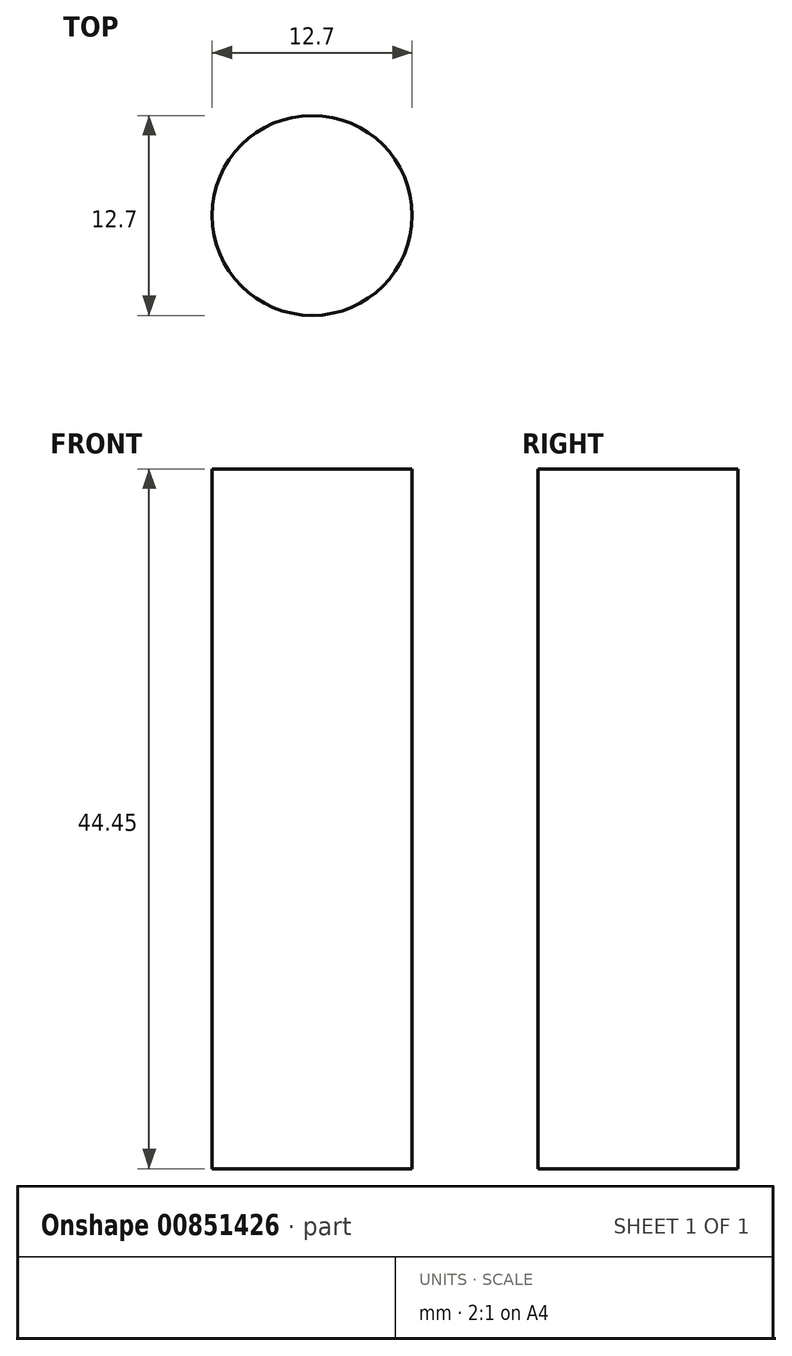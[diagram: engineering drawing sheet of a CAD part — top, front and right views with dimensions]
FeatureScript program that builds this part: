
annotation { "Feature Type Name" : "Feature", "Feature Type Description" : "" }
export const myFeature = defineFeature(function(context is Context, id is Id, definition is map)
    precondition{}
    {
        {
            var Q0;
            Q0=qCreatedBy(makeId("Top.planeOp"),FACE);
            var sketch = newSketch(context, id + "F0", { "sketchPlane" : qUnion([Q0])});
            skCircle(sketch, "E0", {"center": v(-0.1, 0.1) * mm, "radius": 6.35 * mm});
            skSolve(sketch);
        }
        {
            var Q0;
            Q0 = qSketchRegion(id + "F0", true);
            extrude(context, id + "F1", {"entities" : qUnion([Q0]), "oppositeDirection" : true, "depth" : 44.45 * mm, "offsetDistance" : 25.4 * mm});
        }
    });
